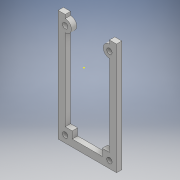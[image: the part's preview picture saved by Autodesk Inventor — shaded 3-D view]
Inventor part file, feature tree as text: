
AUTODESK INVENTOR PART (.ipt)
format: ipt  version: 2017 (Build 210142000, 142)  size: 153,600 bytes
history: native  units: mm
features: other x3, sketch x3, extrude x2
ambient origin geometry x8: Origin, YZ Plane, XZ Plane, XY Plane, X Axis, Y Axis, Z Axis, Center Point
bodies: Solid1 (feature_tree)
feature tree (8):
  other  "k2_t2_base.ipt"
  extrude  "Extrusion5"  Depth=8.0mm
  extrude  "Extrusion7"  Depth=10.0mm TaperAngle=0.0deg
  sketch  "Sketch11"  dims[d67=4.0mm d69=4.0mm d71=4.0mm d72=4.0mm d73=8.0mm d95=3.5mm d96=3.5mm d97=4.0mm d98=4.0mm d99=4.0mm d100=3.5mm d101=3.5mm]
  other  "Solid1::k2_t2_base.ipt"
  other  "TaggingFeature2"
  sketch  "Sketch7"  dims[d21=10.0mm d43=8.0mm]
  sketch  "Sketch8"  dims[d44=10.0mm d45=0.0mm d65=10.0mm d66=0.0mm]
